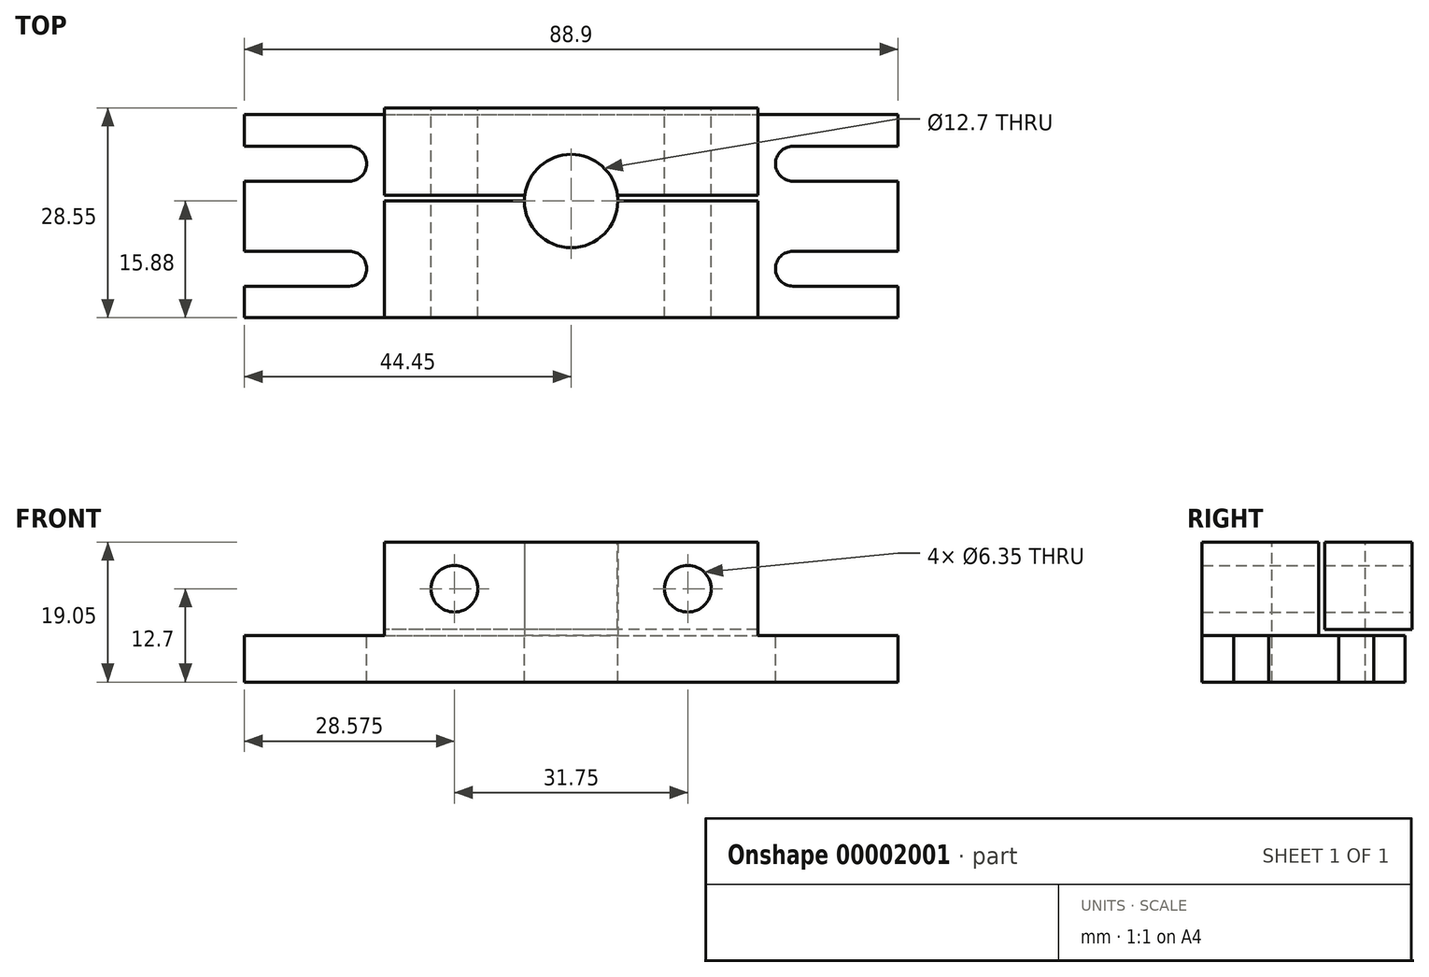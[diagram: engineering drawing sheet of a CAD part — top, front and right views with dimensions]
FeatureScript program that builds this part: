
annotation { "Feature Type Name" : "Feature", "Feature Type Description" : "" }
export const myFeature = defineFeature(function(context is Context, id is Id, definition is map)
    precondition{}
    {
        {
            var Q0;
            Q0=qCreatedBy(makeId("Top.planeOp"),FACE);
            var sketch = newSketch(context, id + "F0", { "sketchPlane" : qUnion([Q0])});
            skLineSegment(sketch, "E0.bottom", {"start": v(-44.45, 12.7) * mm, "end": v(44.45, 12.7) * mm});
            skLineSegment(sketch, "E0.top", {"start": v(-44.45, -12.7) * mm, "end": v(44.45, -12.7) * mm});
            skLineSegment(sketch, "E0.left", {"start": v(-44.45, 12.7) * mm, "end": v(-44.45, -12.7) * mm});
            skLineSegment(sketch, "E0.right", {"start": v(44.45, 12.7) * mm, "end": v(44.45, -12.7) * mm});
            skLineSegment(sketch, "E1", {"start": v(0, 12.7) * mm, "end": v(0, 0) * mm, "construction": true});
            skLineSegment(sketch, "E2", {"start": v(0, 0) * mm, "end": v(-44.45, 0) * mm, "construction": true});
            skSolve(sketch);
        }
        {
            var Q0;
            Q0=qSketchRegion(id+"F0",true);
            extrude(context, id + "F1", {"entities" : qUnion([Q0]), "depth" : 19.05 * mm});
        }
        {
            var Q0;
            Q0=makeQuery(id+"F1.opExtrude","SWEPT_FACE",FACE,{"disambiguationData":[OSD([sQuery(id+"F0.wireOp",EDGE,"E0.top")])]});
            var sketch = newSketch(context, id + "F2", { "sketchPlane" : qUnion([Q0])});
            skLineSegment(sketch, "E3.bottom", {"start": v(25.4, 19.05) * mm, "end": v(44.45, 19.05) * mm});
            skLineSegment(sketch, "E3.top", {"start": v(25.4, 6.35) * mm, "end": v(44.45, 6.35) * mm});
            skLineSegment(sketch, "E3.left", {"start": v(25.4, 19.05) * mm, "end": v(25.4, 6.35) * mm});
            skLineSegment(sketch, "E3.right", {"start": v(44.45, 19.05) * mm, "end": v(44.45, 6.35) * mm});
            skLineSegment(sketch, "E4.0.MirrorCS", {"start": v(-44.45, 19.05) * mm, "end": v(-44.45, 6.35) * mm});
            skLineSegment(sketch, "E4.1.MirrorCS", {"start": v(-25.4, 19.05) * mm, "end": v(-25.4, 6.35) * mm});
            skLineSegment(sketch, "E4.2.MirrorCS", {"start": v(-25.4, 19.05) * mm, "end": v(-44.45, 19.05) * mm});
            skLineSegment(sketch, "E4.3.MirrorCS", {"start": v(-25.4, 6.35) * mm, "end": v(-44.45, 6.35) * mm});
            skSolve(sketch);
        }
        {
            var Q0;
            Q0=qSketchRegion(id+"F2",true);
            var Q1;
            Q1=makeQuery(id+"F1.opExtrude","SWEPT_FACE",FACE,{"disambiguationData":[OSD([sQuery(id+"F0.wireOp",EDGE,"E0.bottom")])]});
            extrude(context, id + "F3", {"entities" : qUnion([Q0]), "operationType" : NewBodyOperationType.REMOVE, "endBound" : BoundingType.UP_TO_SURFACE, "oppositeDirection" : true, "endBoundEntityFace" : qUnion([Q1]), "depth" : 25.4 * mm});
        }
        {
            var Q0;
            Q0=makeQuery(id+"F3.boolean.opBoolean","COPY",FACE,{"derivedFrom":makeQuery(id+"F3.opExtrude","SWEPT_FACE",FACE,{"disambiguationData":[OSD([sQuery(id+"F2.wireOp",EDGE,"E3.left")])]})});
            var sketch = newSketch(context, id + "F4", { "sketchPlane" : qUnion([Q0])});
            skLineSegment(sketch, "E5.bottom", {"start": v(6.35, 19.05) * mm, "end": v(12.7, 19.05) * mm});
            skLineSegment(sketch, "E5.top", {"start": v(6.35, 6.35) * mm, "end": v(12.7, 6.35) * mm});
            skLineSegment(sketch, "E5.left", {"start": v(6.35, 19.05) * mm, "end": v(6.35, 6.35) * mm});
            skLineSegment(sketch, "E5.right", {"start": v(12.7, 19.05) * mm, "end": v(12.7, 6.35) * mm});
            skSolve(sketch);
        }
        {
            var Q0;
            Q0=qSketchRegion(id+"F4",true);
            var Q1;
            Q1=makeQuery(id+"F3.boolean.opBoolean","COPY",FACE,{"derivedFrom":makeQuery(id+"F3.opExtrude","SWEPT_FACE",FACE,{"disambiguationData":[OSD([sQuery(id+"F2.wireOp",EDGE,"E4.1.MirrorCS")])]})});
            extrude(context, id + "F5", {"entities" : qUnion([Q0]), "operationType" : NewBodyOperationType.REMOVE, "endBound" : BoundingType.UP_TO_SURFACE, "oppositeDirection" : true, "endBoundEntityFace" : qUnion([Q1]), "depth" : 25.4 * mm});
        }
        {
            var Q0;
            Q0=makeQuery(id+"F1.opExtrude","SWEPT_FACE",FACE,{"disambiguationData":[OSD([sQuery(id+"F0.wireOp",EDGE,"E0.bottom")])]});
            extrude(context, id + "F6", {"entities" : qUnion([Q0]), "operationType" : NewBodyOperationType.ADD, "depth" : 1.59 * mm});
        }
        {
            var Q0;
            {var subQ0=sQuery(id+"F2.wireOp",EDGE,"E3.top");var subQ1=sQuery(id+"F2.wireOp",EDGE,"E4.3.MirrorCS");var subQ2=sQuery(id+"F4.wireOp",EDGE,"E5.top");Q0=makeQuery(id+"F6.boolean.opBoolean","MERGE",FACE,{"derivedFrom":[makeQuery(id+"F5.boolean.opBoolean","MERGE",FACE,{"derivedFrom":[makeQuery(id+"F3.boolean.opBoolean","COPY",FACE,{"derivedFrom":makeQuery(id+"F3.opExtrude","SWEPT_FACE",FACE,{"disambiguationData":[OSD([subQ0])]})}),makeQuery(id+"F3.boolean.opBoolean","COPY",FACE,{"derivedFrom":makeQuery(id+"F3.opExtrude","SWEPT_FACE",FACE,{"disambiguationData":[OSD([subQ1])]})}),makeQuery(id+"F5.opExtrude","SWEPT_FACE",FACE,{"disambiguationData":[OSD([subQ2])]})]}),makeQuery(id+"F6.opExtrude","SWEPT_FACE",FACE,{"disambiguationData":[OSD([subQ0,subQ1,subQ2,sQuery(id+"F4.wireOp",EDGE,"E5.right")])]})]});}
            var sketch = newSketch(context, id + "F7", { "sketchPlane" : qUnion([Q0])});
            skCircle(sketch, "E6", {"center": v(0, 6.35) * mm, "radius": 6.35 * mm});
            skSolve(sketch);
        }
        {
            var Q0;
            Q0=qSketchRegion(id+"F7",true);
            var Q1;
            {var subQ0=sQuery(id+"F0.wireOp",EDGE,"E0.bottom");Q1=makeQuery(id+"F6.boolean.opBoolean","MERGE",FACE,{"derivedFrom":[makeQuery(id+"F1.opExtrude","CAP_FACE",FACE,{"disambiguationData":[OSD([subQ0,sQuery(id+"F0.wireOp",EDGE,"E0.top"),sQuery(id+"F0.wireOp",EDGE,"E0.left"),sQuery(id+"F0.wireOp",EDGE,"E0.right")])],"isStart":true}),makeQuery(id+"F6.opExtrude","SWEPT_FACE",FACE,{"disambiguationData":[OSD([subQ0])]})]});}
            extrude(context, id + "F8", {"entities" : qUnion([Q0]), "operationType" : NewBodyOperationType.REMOVE, "endBound" : BoundingType.UP_TO_SURFACE, "oppositeDirection" : true, "endBoundEntityFace" : qUnion([Q1]), "depth" : 25.4 * mm});
        }
        {
            var Q0;
            Q0=qSketchRegion(id+"F7",true);
            var Q1;
            Q1=makeQuery(id+"F1.opExtrude","CAP_FACE",FACE,{"disambiguationData":[OSD([sQuery(id+"F0.wireOp",EDGE,"E0.bottom"),sQuery(id+"F0.wireOp",EDGE,"E0.top"),sQuery(id+"F0.wireOp",EDGE,"E0.left"),sQuery(id+"F0.wireOp",EDGE,"E0.right")])],"isStart":false});
            extrude(context, id + "F9", {"entities" : qUnion([Q0]), "operationType" : NewBodyOperationType.REMOVE, "endBound" : BoundingType.UP_TO_SURFACE, "endBoundEntityFace" : qUnion([Q1]), "depth" : 25.4 * mm});
        }
        {
            var Q0;
            Q0=makeQuery(id+"F9.boolean.opBoolean","SPLIT",FACE,{"disambiguationData":[TD([makeQuery(id+"F3.boolean.opBoolean","COPY",FACE,{"derivedFrom":makeQuery(id+"F3.opExtrude","SWEPT_FACE",FACE,{"disambiguationData":[OSD([sQuery(id+"F2.wireOp",EDGE,"E3.left")])]})})])],"derivedFrom":makeQuery(id+"F5.boolean.opBoolean","COPY",FACE,{"derivedFrom":makeQuery(id+"F5.opExtrude","SWEPT_FACE",FACE,{"disambiguationData":[OSD([sQuery(id+"F4.wireOp",EDGE,"E5.left")])]})})});
            var sketch = newSketch(context, id + "F10", { "sketchPlane" : qUnion([Q0])});
            skCircle(sketch, "E7", {"center": v(-15.87, 12.7) * mm, "radius": 3.18 * mm});
            skLineSegment(sketch, "E8", {"start": v(-25.4, 12.7) * mm, "end": v(-15.87, 12.7) * mm, "construction": true});
            skLineSegment(sketch, "E9", {"start": v(-15.87, 19.05) * mm, "end": v(-15.87, 12.7) * mm, "construction": true});
            skCircle(sketch, "E10.0.MirrorC", {"center": v(15.87, 12.7) * mm, "radius": 3.18 * mm});
            skSolve(sketch);
        }
        {
            var Q0;
            Q0=qSketchRegion(id+"F10",true);
            var Q1;
            Q1=makeQuery(id+"F1.opExtrude","SWEPT_FACE",FACE,{"disambiguationData":[OSD([sQuery(id+"F0.wireOp",EDGE,"E0.top")])]});
            extrude(context, id + "F11", {"entities" : qUnion([Q0]), "operationType" : NewBodyOperationType.REMOVE, "endBound" : BoundingType.UP_TO_SURFACE, "oppositeDirection" : true, "endBoundEntityFace" : qUnion([Q1]), "depth" : 25.4 * mm});
        }
        {
            var Q0;
            Q0=makeQuery(id+"F9.boolean.opBoolean","SPLIT",FACE,{"disambiguationData":[TD([makeQuery(id+"F3.boolean.opBoolean","COPY",FACE,{"derivedFrom":makeQuery(id+"F3.opExtrude","SWEPT_FACE",FACE,{"disambiguationData":[OSD([sQuery(id+"F2.wireOp",EDGE,"E3.left")])]})})])],"derivedFrom":makeQuery(id+"F5.boolean.opBoolean","COPY",FACE,{"derivedFrom":makeQuery(id+"F5.opExtrude","SWEPT_FACE",FACE,{"disambiguationData":[OSD([sQuery(id+"F4.wireOp",EDGE,"E5.left")])]})})});
            cPlane(context, id + "F12", {"entities" : qUnion([Q0]), "cplaneType" : CPlaneType.OFFSET, "offset" : 0.79 * mm, "width" : 152.4 * mm, "height" : 152.4 * mm});
        }
        {
            var Q0;
            Q0=qCreatedBy(id+"F12.planeOp",FACE);
            var sketch = newSketch(context, id + "F13", { "sketchPlane" : qUnion([Q0])});
            skLineSegment(sketch, "E11.bottom", {"start": v(-25.4, 19.05) * mm, "end": v(25.4, 19.05) * mm});
            skLineSegment(sketch, "E11.top", {"start": v(-25.4, 7.14) * mm, "end": v(25.4, 7.14) * mm});
            skLineSegment(sketch, "E11.left", {"start": v(-25.4, 19.05) * mm, "end": v(-25.4, 7.14) * mm});
            skLineSegment(sketch, "E11.right", {"start": v(25.4, 19.05) * mm, "end": v(25.4, 7.14) * mm});
            skSolve(sketch);
        }
        {
            var Q0;
            Q0=qSketchRegion(id+"F13",true);
            extrude(context, id + "F14", {"entities" : qUnion([Q0]), "depth" : 11.9 * mm});
        }
        {
            var Q0;
            Q0=makeQuery(id+"F14.opExtrude","SWEPT_FACE",FACE,{"disambiguationData":[OSD([sQuery(id+"F13.wireOp",EDGE,"E11.bottom")])]});
            var sketch = newSketch(context, id + "F15", { "sketchPlane" : qUnion([Q0])});
            skArc(sketch, "E12", {"start": v(6.3, 7.14) * mm, "mid": v(0, 12.7) * mm, "end": v(-6.3, 7.14) * mm});
            skLineSegment(sketch, "E13", {"start": v(-6.3, 7.14) * mm, "end": v(6.3, 7.14) * mm});
            skSolve(sketch);
        }
        {
            var Q0;
            Q0=qSketchRegion(id+"F15",true);
            var Q1;
            Q1=makeQuery(id+"F14.opExtrude","SWEPT_FACE",FACE,{"disambiguationData":[OSD([sQuery(id+"F13.wireOp",EDGE,"E11.top")])]});
            extrude(context, id + "F16", {"entities" : qUnion([Q0]), "operationType" : NewBodyOperationType.REMOVE, "endBound" : BoundingType.UP_TO_SURFACE, "oppositeDirection" : true, "endBoundEntityFace" : qUnion([Q1]), "depth" : 25.4 * mm});
        }
        {
            var Q0;
            Q0=makeQuery(id+"F14.opExtrude","CAP_FACE",FACE,{"disambiguationData":[OSD([sQuery(id+"F13.wireOp",EDGE,"E11.bottom"),sQuery(id+"F13.wireOp",EDGE,"E11.top"),sQuery(id+"F13.wireOp",EDGE,"E11.left"),sQuery(id+"F13.wireOp",EDGE,"E11.right")])],"isStart":false});
            var sketch = newSketch(context, id + "F17", { "sketchPlane" : qUnion([Q0])});
            skCircle(sketch, "E14", {"center": v(-15.87, 12.7) * mm, "radius": 3.18 * mm});
            skCircle(sketch, "E15", {"center": v(15.87, 12.7) * mm, "radius": 3.18 * mm});
            skSolve(sketch);
        }
        {
            var Q0;
            Q0=qSketchRegion(id+"F17",true);
            var Q1;
            {var subQ0=sQuery(id+"F13.wireOp",EDGE,"E11.bottom");var subQ1=sQuery(id+"F13.wireOp",EDGE,"E11.top");var subQ2=sQuery(id+"F13.wireOp",EDGE,"E11.left");Q1=makeQuery(id+"F16.boolean.opBoolean","SPLIT",FACE,{"disambiguationData":[TD([makeQuery(id+"F14.opExtrude","SWEPT_FACE",FACE,{"disambiguationData":[OSD([subQ2])]})])],"derivedFrom":makeQuery(id+"F14.opExtrude","CAP_FACE",FACE,{"disambiguationData":[OSD([subQ0,subQ1,subQ2,sQuery(id+"F13.wireOp",EDGE,"E11.right")])],"isStart":true})});}
            extrude(context, id + "F18", {"entities" : qUnion([Q0]), "operationType" : NewBodyOperationType.REMOVE, "endBound" : BoundingType.UP_TO_SURFACE, "oppositeDirection" : true, "endBoundEntityFace" : qUnion([Q1]), "depth" : 25.4 * mm});
        }
        {
            var Q0;
            Q0=makeQuery(id+"F1.opExtrude","SWEPT_FACE",FACE,{"disambiguationData":[OSD([sQuery(id+"F0.wireOp",EDGE,"E0.top")])]});
            extrude(context, id + "F19", {"entities" : qUnion([Q0]), "operationType" : NewBodyOperationType.REMOVE, "oppositeDirection" : true, "depth" : 3.17 * mm});
        }
        {
            var Q0;
            Q0=makeQuery(id+"F6.opExtrude","CAP_FACE",FACE,{"disambiguationData":[OSD([sQuery(id+"F0.wireOp",EDGE,"E0.bottom")])],"isStart":false});
            extrude(context, id + "F20", {"entities" : qUnion([Q0]), "operationType" : NewBodyOperationType.ADD, "depth" : 3.8 * mm});
        }
        {
            var Q0;
            {var subQ0=sQuery(id+"F2.wireOp",EDGE,"E3.top");var subQ1=sQuery(id+"F2.wireOp",EDGE,"E4.3.MirrorCS");var subQ2=sQuery(id+"F4.wireOp",EDGE,"E5.top");Q0=makeQuery(id+"F6.boolean.opBoolean","MERGE",FACE,{"derivedFrom":[makeQuery(id+"F5.boolean.opBoolean","MERGE",FACE,{"derivedFrom":[makeQuery(id+"F3.boolean.opBoolean","COPY",FACE,{"derivedFrom":makeQuery(id+"F3.opExtrude","SWEPT_FACE",FACE,{"disambiguationData":[OSD([subQ0])]})}),makeQuery(id+"F3.boolean.opBoolean","COPY",FACE,{"derivedFrom":makeQuery(id+"F3.opExtrude","SWEPT_FACE",FACE,{"disambiguationData":[OSD([subQ1])]})}),makeQuery(id+"F5.opExtrude","SWEPT_FACE",FACE,{"disambiguationData":[OSD([subQ2])]})]}),makeQuery(id+"F6.opExtrude","SWEPT_FACE",FACE,{"disambiguationData":[OSD([subQ0,subQ1,subQ2,sQuery(id+"F4.wireOp",EDGE,"E5.right")])]})]});}
            var sketch = newSketch(context, id + "F21", { "sketchPlane" : qUnion([Q0])});
            skLineSegment(sketch, "E16", {"start": v(-44.45, -0.48) * mm, "end": v(-44.45, -5.23) * mm});
            skLineSegment(sketch, "E17", {"start": v(-44.45, -5.23) * mm, "end": v(-30.18, -5.23) * mm});
            skArc(sketch, "E18", {"start": v(-30.18, -5.23) * mm, "mid": v(-27.8, -2.85) * mm, "end": v(-30.18, -0.48) * mm});
            skLineSegment(sketch, "E19", {"start": v(-44.45, -0.48) * mm, "end": v(-30.18, -0.48) * mm});
            skLineSegment(sketch, "E20", {"start": v(-44.45, 13.8) * mm, "end": v(-44.45, 9.05) * mm});
            skLineSegment(sketch, "E21", {"start": v(-44.45, 9.05) * mm, "end": v(-30.18, 9.05) * mm});
            skLineSegment(sketch, "E22", {"start": v(-44.45, 13.8) * mm, "end": v(-30.18, 13.8) * mm});
            skArc(sketch, "E23", {"start": v(-30.18, 9.05) * mm, "mid": v(-27.8, 11.42) * mm, "end": v(-30.18, 13.8) * mm});
            skLineSegment(sketch, "E24", {"start": v(-44.45, 4.29) * mm, "end": v(-25.4, 4.29) * mm, "construction": true});
            skLineSegment(sketch, "E25", {"start": v(44.45, 13.8) * mm, "end": v(44.45, 9.05) * mm});
            skLineSegment(sketch, "E26", {"start": v(44.45, 9.05) * mm, "end": v(30.18, 9.05) * mm});
            skLineSegment(sketch, "E27", {"start": v(44.45, 13.8) * mm, "end": v(30.18, 13.8) * mm});
            skLineSegment(sketch, "E28", {"start": v(30.18, -0.48) * mm, "end": v(44.45, -0.48) * mm});
            skLineSegment(sketch, "E29", {"start": v(44.45, -0.48) * mm, "end": v(44.45, -5.23) * mm});
            skLineSegment(sketch, "E30", {"start": v(44.45, -5.23) * mm, "end": v(30.18, -5.23) * mm});
            skArc(sketch, "E31", {"start": v(30.18, 13.8) * mm, "mid": v(27.8, 11.42) * mm, "end": v(30.18, 9.05) * mm});
            skArc(sketch, "E32", {"start": v(30.18, -0.48) * mm, "mid": v(27.8, -2.85) * mm, "end": v(30.18, -5.23) * mm});
            skSolve(sketch);
        }
        {
            var Q0;
            Q0=qSketchRegion(id+"F21",true);
            var Q1;
            {var subQ0=sQuery(id+"F0.wireOp",EDGE,"E0.bottom");Q1=makeQuery(id+"F6.boolean.opBoolean","MERGE",FACE,{"derivedFrom":[makeQuery(id+"F1.opExtrude","CAP_FACE",FACE,{"disambiguationData":[OSD([subQ0,sQuery(id+"F0.wireOp",EDGE,"E0.top"),sQuery(id+"F0.wireOp",EDGE,"E0.left"),sQuery(id+"F0.wireOp",EDGE,"E0.right")])],"isStart":true}),makeQuery(id+"F6.opExtrude","SWEPT_FACE",FACE,{"disambiguationData":[OSD([subQ0])]})]});}
            extrude(context, id + "F22", {"entities" : qUnion([Q0]), "operationType" : NewBodyOperationType.REMOVE, "endBound" : BoundingType.UP_TO_SURFACE, "oppositeDirection" : true, "endBoundEntityFace" : qUnion([Q1]), "depth" : 25.4 * mm});
        }
    });
